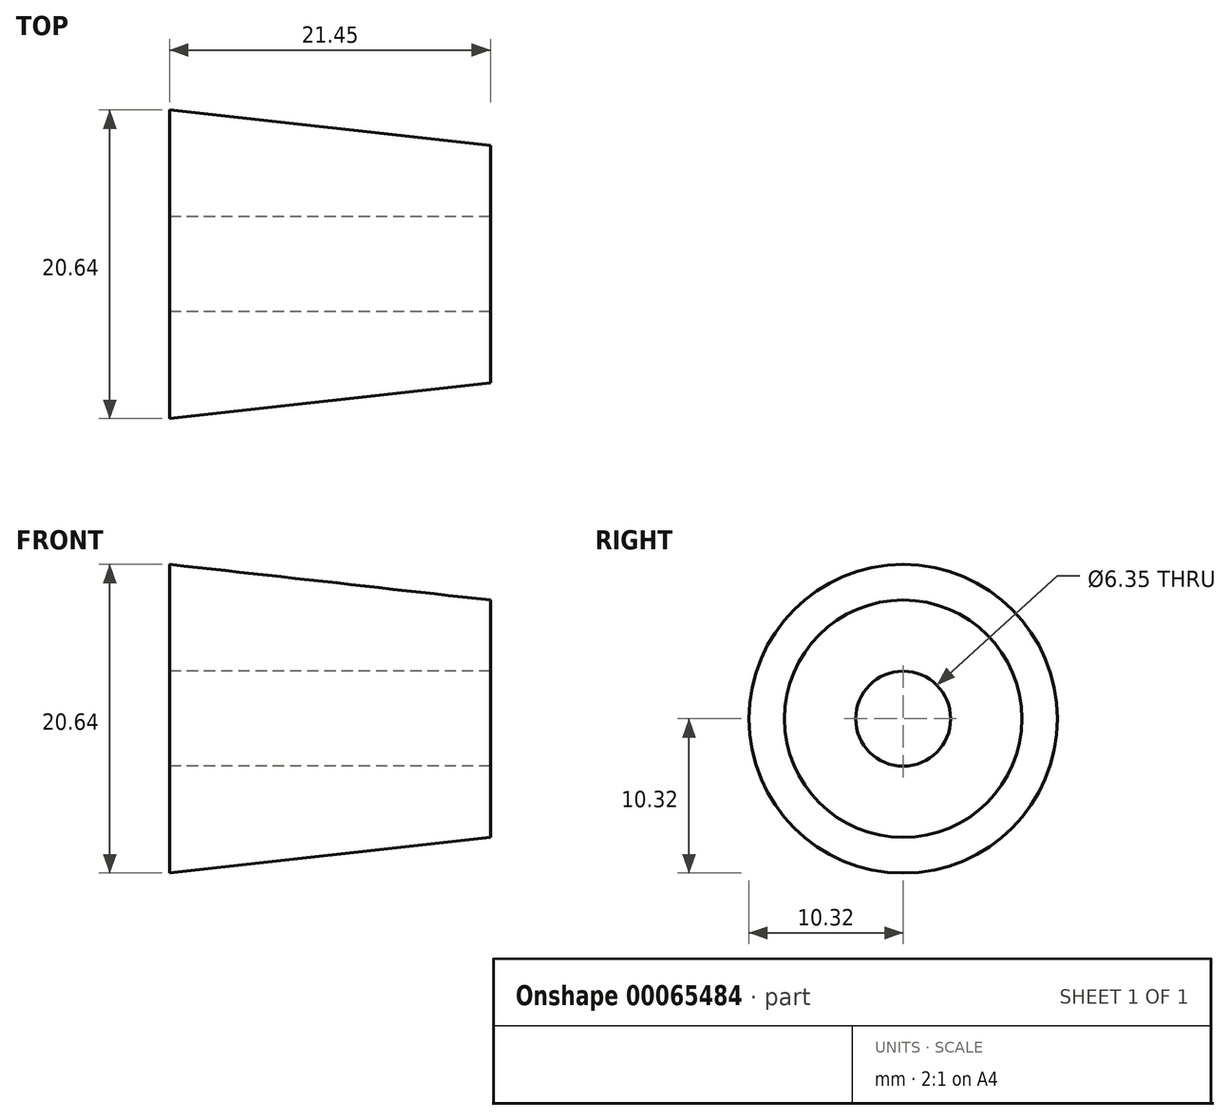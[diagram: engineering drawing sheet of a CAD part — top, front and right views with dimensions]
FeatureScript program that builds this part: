
annotation { "Feature Type Name" : "Feature", "Feature Type Description" : "" }
export const myFeature = defineFeature(function(context is Context, id is Id, definition is map)
    precondition{}
    {
        {
            var Q0;
            Q0=qCreatedBy(makeId("Front.planeOp"),FACE);
            var sketch = newSketch(context, id + "F0", { "sketchPlane" : qUnion([Q0])});
            skLineSegment(sketch, "E0", {"start": v(-24.8, 16.82) * mm, "end": v(-24.8, -3.82) * mm});
            skLineSegment(sketch, "E1", {"start": v(-24.8, 6.5) * mm, "end": v(-3.35, 6.5) * mm});
            skLineSegment(sketch, "E2", {"start": v(-3.35, 6.5) * mm, "end": v(-3.35, -1.44) * mm});
            skLineSegment(sketch, "E3", {"start": v(-3.35, 6.5) * mm, "end": v(-3.35, 14.44) * mm});
            skLineSegment(sketch, "E4", {"start": v(-24.8, 16.82) * mm, "end": v(-3.35, 14.44) * mm});
            skLineSegment(sketch, "E5", {"start": v(-24.8, -3.82) * mm, "end": v(-3.35, -1.44) * mm});
            skSolve(sketch);
        }
        {
            var Q0;
            {var subQ2=sQuery(id+"F0.wireOp",EDGE,"E1");Q0=makeQuery(id+"F0.imprint","IMPRINT",FACE,{"disambiguationData":[TD([[makeQuery(id+"F0.imprint","IMPRINT",EDGE,{"derivedFrom":subQ2}),1.0]])]});}
            var Q1;
            Q1=sQuery(id+"F0.wireOp",EDGE,"E1");
            revolve(context, id + "F1", {"entities" : qUnion([Q0]), "axis" : qUnion([Q1]), "revolveType" : RevolveType.FULL});
        }
        {
            var Q0;
            Q0=makeQuery(id+"F1.opRevolve","SWEPT_FACE",FACE,{"disambiguationData":[OSD([sQuery(id+"F0.wireOp",EDGE,"E0")])]});
            var sketch = newSketch(context, id + "F2", { "sketchPlane" : qUnion([Q0])});
            skCircle(sketch, "E6", {"center": v(0, 6.5) * mm, "radius": 3.18 * mm});
            skSolve(sketch);
        }
        {
            var Q0;
            Q0=makeQuery(id+"F2.imprint","IMPRINT",FACE,{"disambiguationData":[TD([[makeQuery(id+"F2.imprint","IMPRINT",EDGE,{"derivedFrom":sQuery(id+"F2.wireOp",EDGE,"E6")}),1.0]])]});
            extrude(context, id + "F3", {"entities" : qUnion([Q0]), "operationType" : NewBodyOperationType.REMOVE, "oppositeDirection" : true, "depth" : 25.4 * mm});
        }
    });
